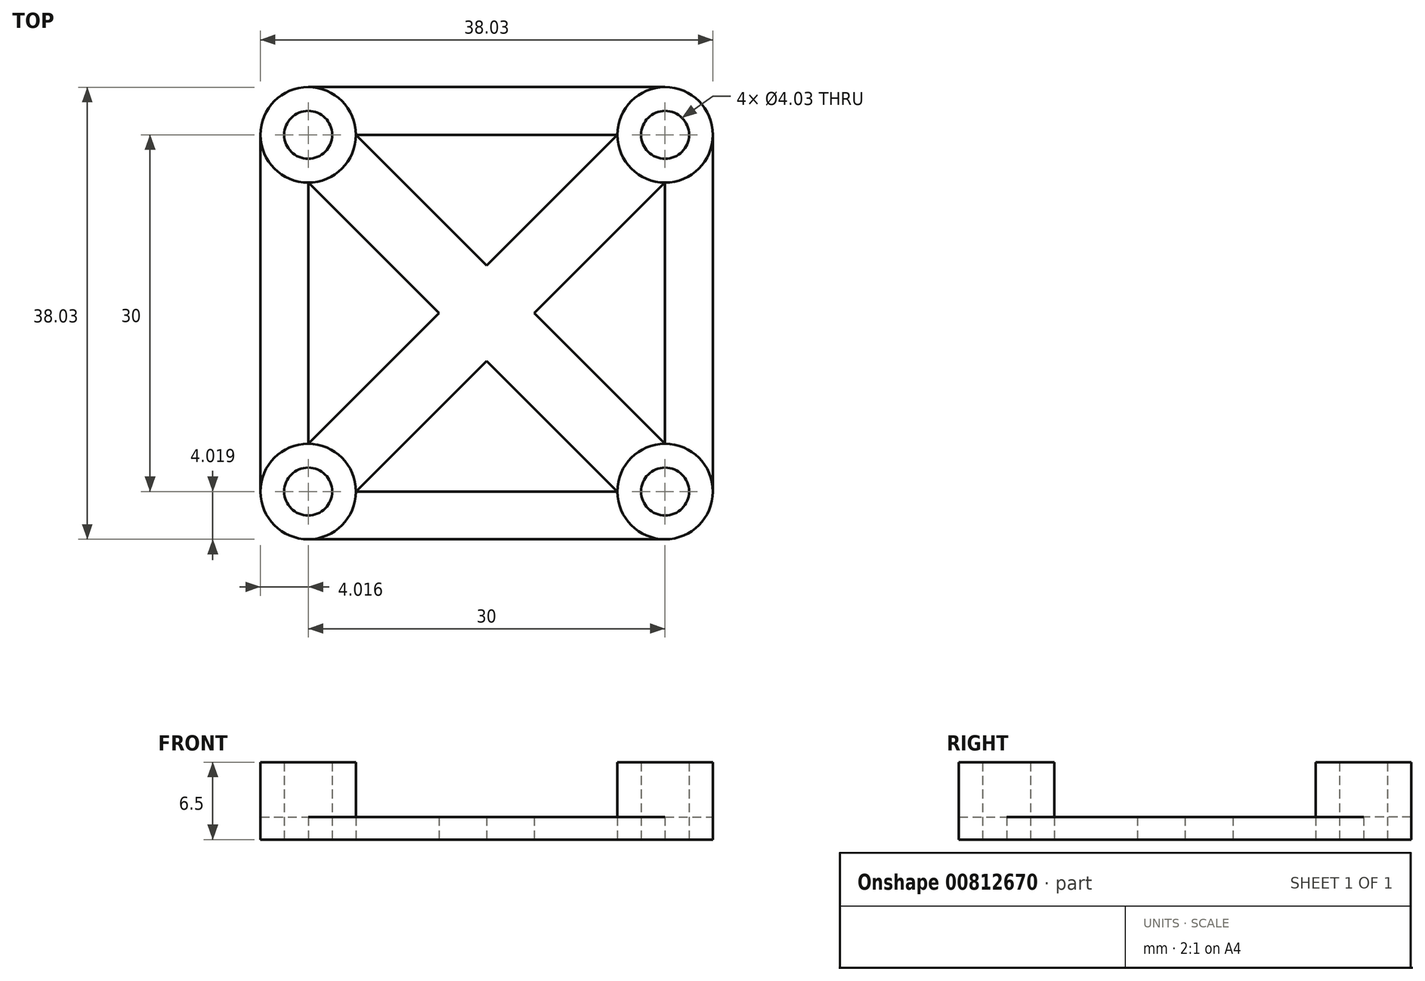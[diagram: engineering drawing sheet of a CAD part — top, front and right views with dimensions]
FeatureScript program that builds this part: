
annotation { "Feature Type Name" : "Feature", "Feature Type Description" : "" }
export const myFeature = defineFeature(function(context is Context, id is Id, definition is map)
    precondition{}
    {
        {
            var Q0;
            Q0=qCreatedBy(makeId("Top.planeOp"),FACE);
            var sketch = newSketch(context, id + "F0", { "sketchPlane" : qUnion([Q0])});
            skLineSegment(sketch, "E0.bottom", {"start": v(-12.91, 5.9) * mm, "end": v(17.09, 5.9) * mm});
            skLineSegment(sketch, "E0.top", {"start": v(-12.91, -24.1) * mm, "end": v(17.09, -24.1) * mm});
            skLineSegment(sketch, "E0.left", {"start": v(-12.91, 5.9) * mm, "end": v(-12.91, -24.1) * mm});
            skLineSegment(sketch, "E0.right", {"start": v(17.09, 5.9) * mm, "end": v(17.09, -24.1) * mm});
            skCircle(sketch, "E1", {"center": v(17.09, 5.9) * mm, "radius": 2.02 * mm});
            skCircle(sketch, "E2", {"center": v(-12.91, 5.9) * mm, "radius": 2.02 * mm});
            skCircle(sketch, "E3", {"center": v(-12.91, -24.1) * mm, "radius": 2.02 * mm});
            skCircle(sketch, "E4", {"center": v(17.09, -24.1) * mm, "radius": 2.02 * mm});
            skCircle(sketch, "E5", {"center": v(17.09, -24.1) * mm, "radius": 4.01 * mm});
            skCircle(sketch, "E6", {"center": v(17.09, 5.9) * mm, "radius": 4.01 * mm});
            skCircle(sketch, "E7", {"center": v(-12.91, 5.9) * mm, "radius": 4.01 * mm});
            skCircle(sketch, "E8", {"center": v(-12.91, -24.1) * mm, "radius": 4.01 * mm});
            skLineSegment(sketch, "E9", {"start": v(-12.91, 9.91) * mm, "end": v(17.09, 9.91) * mm});
            skLineSegment(sketch, "E10", {"start": v(21.1, 5.9) * mm, "end": v(21.1, -24.1) * mm});
            skLineSegment(sketch, "E11", {"start": v(17.09, -28.12) * mm, "end": v(-12.91, -28.12) * mm});
            skLineSegment(sketch, "E12", {"start": v(-16.93, -24.1) * mm, "end": v(-16.93, 5.9) * mm});
            skLineSegment(sketch, "E13", {"start": v(-12.91, 1.88) * mm, "end": v(13.07, -24.1) * mm});
            skLineSegment(sketch, "E14", {"start": v(-8.9, 5.9) * mm, "end": v(17.09, -20.09) * mm});
            skLineSegment(sketch, "E15", {"start": v(13.07, 5.9) * mm, "end": v(-12.91, -20.09) * mm});
            skLineSegment(sketch, "E16", {"start": v(-8.9, -24.1) * mm, "end": v(17.09, 1.88) * mm});
            skSolve(sketch);
        }
        {
            var Q0;
            {var subQ0=sQuery(id+"F0.wireOp",EDGE,"E2");var subQ1=sQuery(id+"F0.wireOp",EDGE,"E0.bottom");var subQ2=makeQuery(id+"F0.imprint","INTERSECT",VERTEX,{"derivedFrom":[subQ1,subQ0]});Q0=makeQuery(id+"F0.imprint","IMPRINT",FACE,{"disambiguationData":[TD([[makeQuery(id+"F0.imprint","IMPRINT",EDGE,{"disambiguationData":[TD([[subQ2,-1.0]])],"derivedFrom":subQ1}),-1.0]])]});}
            var Q1;
            {var subQ0=sQuery(id+"F0.wireOp",EDGE,"E2");var subQ1=sQuery(id+"F0.wireOp",EDGE,"E0.bottom");var subQ2=makeQuery(id+"F0.imprint","INTERSECT",VERTEX,{"derivedFrom":[subQ1,subQ0]});Q1=makeQuery(id+"F0.imprint","IMPRINT",FACE,{"disambiguationData":[TD([[makeQuery(id+"F0.imprint","IMPRINT",EDGE,{"disambiguationData":[TD([[subQ2,-1.0]])],"derivedFrom":subQ1}),1.0]])]});}
            var Q2;
            {var subQ0=sQuery(id+"F0.wireOp",EDGE,"E6");var subQ4=sQuery(id+"F0.wireOp",EDGE,"E0.bottom");var subQ9=makeQuery(id+"F0.imprint","INTERSECT",VERTEX,{"derivedFrom":[subQ4,subQ0]});Q2=makeQuery(id+"F0.imprint","IMPRINT",FACE,{"disambiguationData":[TD([[makeQuery(id+"F0.imprint","IMPRINT",EDGE,{"disambiguationData":[TD([[subQ9,-1.0]])],"derivedFrom":subQ4}),1.0]])]});}
            var Q3;
            {var subQ0=sQuery(id+"F0.wireOp",EDGE,"E6");var subQ1=sQuery(id+"F0.wireOp",EDGE,"E0.bottom");var subQ2=makeQuery(id+"F0.imprint","INTERSECT",VERTEX,{"derivedFrom":[subQ1,subQ0]});Q3=makeQuery(id+"F0.imprint","IMPRINT",FACE,{"disambiguationData":[TD([[makeQuery(id+"F0.imprint","IMPRINT",EDGE,{"disambiguationData":[TD([[subQ2,-1.0]])],"derivedFrom":subQ1}),-1.0]])]});}
            var Q4;
            {var subQ1=sQuery(id+"F0.wireOp",EDGE,"E0.top");var subQ5=sQuery(id+"F0.wireOp",EDGE,"E5");var subQ8=makeQuery(id+"F0.imprint","INTERSECT",VERTEX,{"derivedFrom":[subQ1,subQ5]});Q4=makeQuery(id+"F0.imprint","IMPRINT",FACE,{"disambiguationData":[TD([[makeQuery(id+"F0.imprint","IMPRINT",EDGE,{"disambiguationData":[TD([[subQ8,-1.0]])],"derivedFrom":subQ1}),-1.0]])]});}
            var Q5;
            {var subQ0=sQuery(id+"F0.wireOp",EDGE,"E5");var subQ1=sQuery(id+"F0.wireOp",EDGE,"E0.top");var subQ2=makeQuery(id+"F0.imprint","INTERSECT",VERTEX,{"derivedFrom":[subQ1,subQ0]});Q5=makeQuery(id+"F0.imprint","IMPRINT",FACE,{"disambiguationData":[TD([[makeQuery(id+"F0.imprint","IMPRINT",EDGE,{"disambiguationData":[TD([[subQ2,-1.0]])],"derivedFrom":subQ1}),1.0]])]});}
            var Q6;
            {var subQ0=sQuery(id+"F0.wireOp",EDGE,"E3");var subQ1=sQuery(id+"F0.wireOp",EDGE,"E0.top");var subQ2=makeQuery(id+"F0.imprint","INTERSECT",VERTEX,{"derivedFrom":[subQ1,subQ0]});Q6=makeQuery(id+"F0.imprint","IMPRINT",FACE,{"disambiguationData":[TD([[makeQuery(id+"F0.imprint","IMPRINT",EDGE,{"disambiguationData":[TD([[subQ2,-1.0]])],"derivedFrom":subQ1}),-1.0]])]});}
            var Q7;
            {var subQ0=sQuery(id+"F0.wireOp",EDGE,"E3");var subQ1=sQuery(id+"F0.wireOp",EDGE,"E0.top");var subQ2=makeQuery(id+"F0.imprint","INTERSECT",VERTEX,{"derivedFrom":[subQ1,subQ0]});Q7=makeQuery(id+"F0.imprint","IMPRINT",FACE,{"disambiguationData":[TD([[makeQuery(id+"F0.imprint","IMPRINT",EDGE,{"disambiguationData":[TD([[subQ2,-1.0]])],"derivedFrom":subQ1}),1.0]])]});}
            extrude(context, id + "F1", {"entities" : qUnion([Q0, Q1, Q2, Q3, Q4, Q5, Q6, Q7]), "depth" : 6.5 * mm, "offsetDistance" : 25 * mm});
        }
        {
            var Q0;
            Q0 = qSketchRegion(id + "F0", true);
            var Q1;
            {var subQ0=sQuery(id+"F0.wireOp",EDGE,"E13");var subQ5=sQuery(id+"F0.wireOp",EDGE,"E15");var subQ6=makeQuery(id+"F0.imprint","INTERSECT",VERTEX,{"derivedFrom":[subQ0,subQ5]});Q1=makeQuery(id+"F0.imprint","IMPRINT",FACE,{"disambiguationData":[TD([[makeQuery(id+"F0.imprint","IMPRINT",EDGE,{"disambiguationData":[TD([[subQ6,1.0]])],"derivedFrom":subQ5}),-1.0]])]});}
            var Q2;
            {var subQ0=sQuery(id+"F0.wireOp",EDGE,"E15");var subQ5=sQuery(id+"F0.wireOp",EDGE,"E14");var subQ6=makeQuery(id+"F0.imprint","INTERSECT",VERTEX,{"derivedFrom":[subQ5,subQ0]});Q2=makeQuery(id+"F0.imprint","IMPRINT",FACE,{"disambiguationData":[TD([[makeQuery(id+"F0.imprint","IMPRINT",EDGE,{"disambiguationData":[TD([[subQ6,-1.0]])],"derivedFrom":subQ5}),1.0]])]});}
            var Q3;
            {var subQ0=sQuery(id+"F0.wireOp",EDGE,"E15");var subQ1=sQuery(id+"F0.wireOp",EDGE,"E13");var subQ2=makeQuery(id+"F0.imprint","INTERSECT",VERTEX,{"derivedFrom":[subQ1,subQ0]});Q3=makeQuery(id+"F0.imprint","IMPRINT",FACE,{"disambiguationData":[TD([[makeQuery(id+"F0.imprint","IMPRINT",EDGE,{"disambiguationData":[TD([[subQ2,-1.0]])],"derivedFrom":subQ1}),1.0]])]});}
            var Q4;
            {var subQ0=sQuery(id+"F0.wireOp",EDGE,"E13");var subQ5=sQuery(id+"F0.wireOp",EDGE,"E16");var subQ6=makeQuery(id+"F0.imprint","INTERSECT",VERTEX,{"derivedFrom":[subQ0,subQ5]});Q4=makeQuery(id+"F0.imprint","IMPRINT",FACE,{"disambiguationData":[TD([[makeQuery(id+"F0.imprint","IMPRINT",EDGE,{"disambiguationData":[TD([[subQ6,-1.0]])],"derivedFrom":subQ5}),-1.0]])]});}
            var Q5;
            {var subQ0=sQuery(id+"F0.wireOp",EDGE,"E15");var subQ5=sQuery(id+"F0.wireOp",EDGE,"E13");var subQ6=makeQuery(id+"F0.imprint","INTERSECT",VERTEX,{"derivedFrom":[subQ5,subQ0]});Q5=makeQuery(id+"F0.imprint","IMPRINT",FACE,{"disambiguationData":[TD([[makeQuery(id+"F0.imprint","IMPRINT",EDGE,{"disambiguationData":[TD([[subQ6,-1.0]])],"derivedFrom":subQ5}),-1.0]])]});}
            extrude(context, id + "F2", {"entities" : qUnion([Q0, Q1, Q2, Q3, Q4, Q5]), "operationType" : NewBodyOperationType.ADD, "depth" : 1.9 * mm, "offsetDistance" : 25 * mm});
        }
    });
